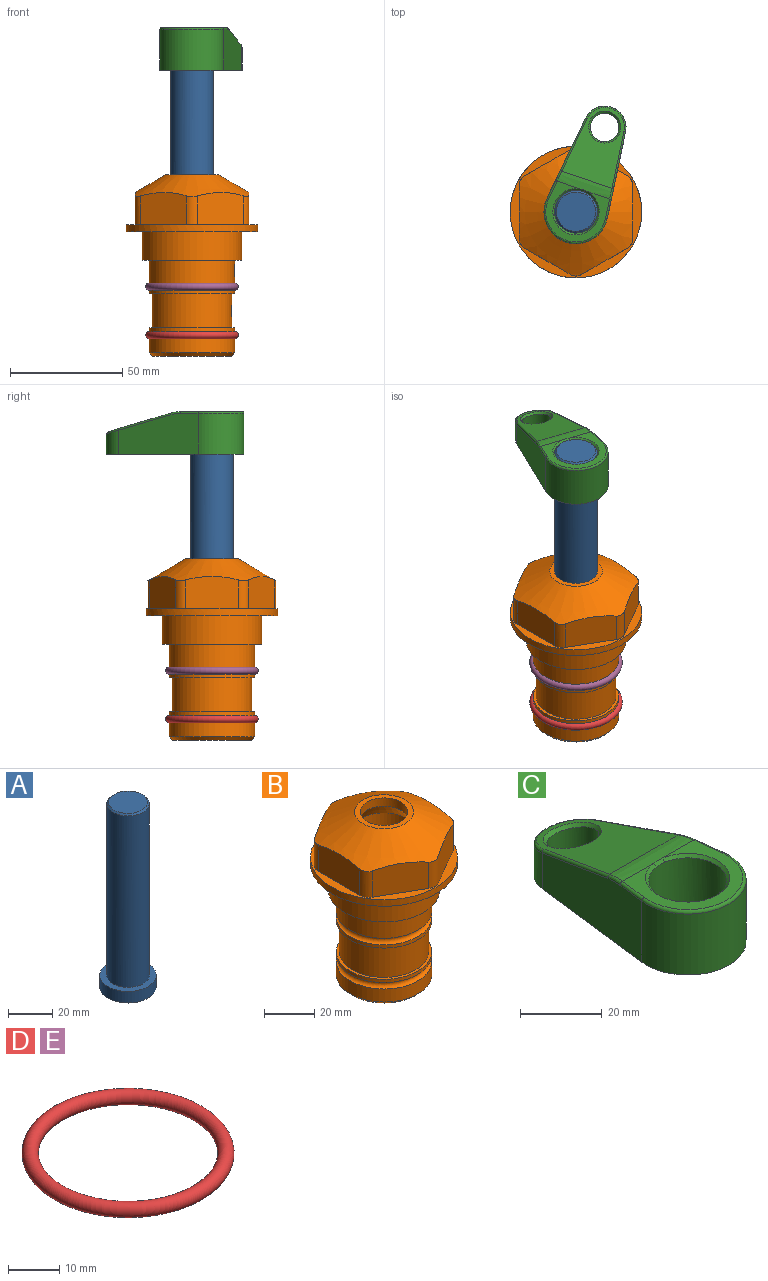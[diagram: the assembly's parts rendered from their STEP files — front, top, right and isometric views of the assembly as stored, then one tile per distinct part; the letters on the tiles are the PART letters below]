
ASSEMBLY  parts=5 mates=4
PART A: 6 faces, bbox 25.4x25.4x101.6 mm
  f0: plane 17.46x17.46mm, normal (0,0,1), area 239.5mm2, adj f5
  f1: plane 25.4x25.4mm, normal (0,0,-1), area 506.7mm2, adj f2
  f2: cylinder r=12.7mm len=25.4mm, axis (0,0,1), area 506.7mm2, adj f1,f3
  f3: plane 25.4x25.4mm, normal (0,0,1), area 221.7mm2, adj f2,f4
  f4: cylinder r=9.53mm len=94.46mm, axis (0,0,1), area 5653mm2, adj f3,f5
  f5: cone r=8.73mm half-angle=45deg, axis (0,0,-1), area 64.4mm2, adj f0,f4
PART B: 36 faces, bbox 58.7x58.7x81 mm
  f0: cylinder r=17.78mm len=35.56mm, axis (0,0,1), area 1670.8mm2, adj f23,f24,f31
  f1: cylinder r=19.05mm len=38.1mm, axis (0,0,1), area 1191.9mm2, adj f26,f27,f30
  f2: plane 58.66x58.66mm, normal (0,0,-1), area 1150.6mm2, adj f3,f28
  f3: cylinder r=29.33mm len=58.66mm, axis (0,0,-1), area 585.1mm2, adj f2,f4
  f4: plane 58.66x58.66mm, normal (0,0,1), area 475.9mm2, adj f3,f5,f6,f7,f8,f9,f10,f11
  f5: plane 20.32x14.34mm, normal (-0.5,0.87,0), area 324.4mm2, adj f4,f15,f16,f17
  f6: plane 20.32x14.34mm, normal (0.5,0.87,0), area 324.4mm2, adj f4,f14,f15,f17
  f7: plane 23.48x14.34mm, normal (1,0,0), area 324.4mm2, adj f4,f13,f14,f17
  f8: plane 20.32x14.34mm, normal (0.5,-0.87,0), area 324.4mm2, adj f4,f12,f13,f17
  f9: plane 20.32x14.34mm, normal (-0.5,-0.87,0), area 324.4mm2, adj f4,f11,f12,f17
  f10: plane 23.48x14.34mm, normal (-1,0,0), area 324.4mm2, adj f4,f11,f16,f17
  f11: cylinder r=5.08mm len=12.85mm, axis (0,0,-1), area 67.2mm2, adj f4,f9,f10,f17
  f12: cylinder r=5.08mm len=12.85mm, axis (0,0,-1), area 67.2mm2, adj f4,f8,f9,f17
  f13: cylinder r=5.08mm len=12.85mm, axis (0,0,-1), area 67.2mm2, adj f4,f7,f8,f17
  f14: cylinder r=5.08mm len=12.85mm, axis (0,0,-1), area 67.2mm2, adj f4,f6,f7,f17
  f15: cylinder r=5.08mm len=12.85mm, axis (0,0,-1), area 67.2mm2, adj f4,f5,f6,f17
  f16: cylinder r=5.08mm len=12.85mm, axis (0,0,-1), area 67.2mm2, adj f4,f5,f10,f17
  f17: cone r=11.73mm half-angle=60deg, axis (0,0,-1), area 2071.8mm2, adj f5,f6,f7,f8,f9,f10,f11,f12
  f18: plane 23.46x23.46mm, normal (0,0,1), area 147.4mm2, adj f17,f35
  f19: plane 34.93x34.93mm, normal (0,0,-1), area 958mm2, adj f29
  f20: cylinder r=19.05mm len=38.1mm, axis (0,0,1), area 760.1mm2, adj f21,f29
  f21: torus R=19.05mm, axis (0,0,1), area 565.3mm2, adj f20,f22
  f22: cylinder r=19.05mm len=38.1mm, axis (0,0,1), area 190mm2, adj f21,f23
  f23: plane 38.1x38.1mm, normal (0,0,1), area 146.9mm2, adj f0,f22
  f24: plane 38.1x38.1mm, normal (0,0,-1), area 146.9mm2, adj f0,f25
  f25: cylinder r=19.05mm len=38.1mm, axis (0,0,1), area 190mm2, adj f24,f26
  f26: torus R=19.05mm, axis (0,0,1), area 565.3mm2, adj f1,f25
  f27: plane 44.45x44.45mm, normal (0,0,-1), area 411.7mm2, adj f1,f28
  f28: cylinder r=22.23mm len=44.45mm, axis (0,0,1), area 1773.5mm2, adj f2,f27
  f29: cone r=19.05mm half-angle=45deg, axis (0,0,1), area 257.5mm2, adj f19,f20
  f30: cylinder r=3.17mm len=6.75mm, axis (-1,0,0), area 128mm2, adj f1,f33
  f31: cylinder r=3.17mm len=6.35mm, axis (-1,0,0), area 102.5mm2, adj f0,f33
  f32: plane 25.4x25.4mm, normal (0,0,1), area 506.7mm2, adj f33
  f33: cylinder r=12.7mm len=66.42mm, axis (0,0,-1), area 5236.2mm2, adj f30,f31,f32,f34
  f34: cone r=9.53mm half-angle=30deg, axis (0,0,-1), area 443.4mm2, adj f33,f35
  f35: cylinder r=9.53mm len=19.05mm, axis (0,0,-1), area 240.9mm2, adj f18,f34
PART C: 31 faces, bbox 31.7x65.5x19.8 mm
  f0: plane 39.12x18.26mm, normal (0.99,0.12,0), area 612.2mm2, adj f1,f4,f7,f11,f13,f15
  f1: cylinder r=9.53mm len=18.91mm, axis (0,0,-1), area 296.1mm2, adj f0,f2,f7,f17
  f2: plane 39.12x18.26mm, normal (-0.99,0.12,0), area 612.2mm2, adj f1,f4,f7,f12,f14,f16
  f3: cylinder r=6.35mm len=12.7mm, axis (0,0,-1), area 362.4mm2, adj f7,f18
  f4: cylinder r=14.29mm len=28.58mm, axis (0,0,-1), area 882.2mm2, adj f0,f2,f7,f10
  f5: cylinder r=9.53mm len=19.05mm, axis (0,0,-1), area 1092.6mm2, adj f7,f19,f20
  f6: plane 26.99x23.69mm, normal (0,0,1), area 216.2mm2, adj f9,f10,f11,f12,f19
  f7: plane 63.5x28.58mm, normal (0,0,-1), area 661.8mm2, adj f0,f1,f2,f3,f4,f5,f22,f23
  f8: plane 33.52x23.6mm, normal (0,0.26,0.97), area 486mm2, adj f9,f15,f16,f17,f18
  f9: cylinder r=19.05mm len=24.72mm, axis (1,0,0), area 120.4mm2, adj f6,f8,f13,f14,f20
  f10: torus R=13.49mm, axis (0,0,1), area 59mm2, adj f4,f6,f11,f12
  f11: cylinder r=0.79mm len=8.67mm, axis (0.12,-0.99,0), area 10.8mm2, adj f0,f6,f10,f13
  f12: cylinder r=0.79mm len=8.67mm, axis (0.12,0.99,0), area 10.8mm2, adj f2,f6,f10,f14
  f13: bspline ~4.95x1.42mm, area 6.1mm2, adj f0,f9,f11,f15
  f14: bspline ~4.95x1.42mm, area 6.1mm2, adj f2,f9,f12,f16
  f15: cylinder r=0.79mm len=25.95mm, axis (0.12,-0.96,0.26), area 32.9mm2, adj f0,f8,f13,f17
  f16: cylinder r=0.79mm len=25.95mm, axis (0.12,0.96,-0.26), area 32.9mm2, adj f2,f8,f14,f17
  f17: bspline ~18.91x8.38mm, area 30mm2, adj f1,f8,f15,f16
  f18: bspline ~14.29x14.29mm, area 48.3mm2, adj f3,f8
  f19: cone r=9.53mm half-angle=45deg, axis (0,0,1), area 66.5mm2, adj f5,f6,f20
  f20: bspline ~3.22x0.96mm, area 3.5mm2, adj f5,f9,f19
  f21: plane 2.75x2.72mm, normal (0,0,-1), area 2.9mm2, adj f23,f25,f28
  f22: plane 23.05x15.88mm, normal (-0.99,-0.12,0), area 323.6mm2, adj f7,f25,f26,f27,f28,f29
  f23: plane 23.05x15.88mm, normal (0.99,-0.12,0), area 323.6mm2, adj f7,f21,f25,f27,f28,f30
  f24: cylinder r=9.53mm len=10.69mm, axis (0,0,-1), area 114.7mm2, adj f7,f27,f29,f30
  f25: cylinder r=12.7mm len=20.59mm, axis (0,0,-1), area 381.1mm2, adj f7,f21,f22,f23,f26,f28
  f26: plane 2.75x2.72mm, normal (0,0,-1), area 2.9mm2, adj f22,f25,f28
  f27: plane 19.72x18.37mm, normal (0,-0.26,-0.97), area 291.8mm2, adj f22,f23,f24,f28,f29,f30
  f28: cylinder r=15.88mm len=19.92mm, axis (1,0,0), area 54.8mm2, adj f21,f22,f23,f25,f26,f27
  f29: cylinder r=1.59mm len=11mm, axis (0,0,-1), area 34.7mm2, adj f7,f22,f24,f27
  f30: cylinder r=1.59mm len=11mm, axis (0,0,-1), area 34.7mm2, adj f7,f23,f24,f27
PART D: 1 faces, bbox 44.7x44.7x3.2 mm
  f0: torus R=19.05mm, axis (0,0,1), area 1193.9mm2
PART E: same geometry as D
PLACE A rot(axis=(0,0,-1),18.8deg) t=(0,0,27.55)mm
PLACE B at identity fixed
PLACE C rot(axis=(0,0,-1),18.8deg) t=(0,0,27.55)mm
PLACE D t=(0,0,-21.59)mm
PLACE E rot(axis=(0,0,1),180deg) t=(0,0,0)mm
MATE fastened E.f0 <-> B.f0  axis (0,0,1) through (0,0,-24.51)mm
MATE cylindrical A.f2 <-> B.f0  axis (0,0,-1) through (0,0,-10.55)mm
MATE fastened D.f0 <-> B.f0  axis (0,0,1) through (0,0,-46.1)mm
MATE fastened C.f4 <-> A.f2  axis (0,0,-1) through (0,0,90.26)mm
